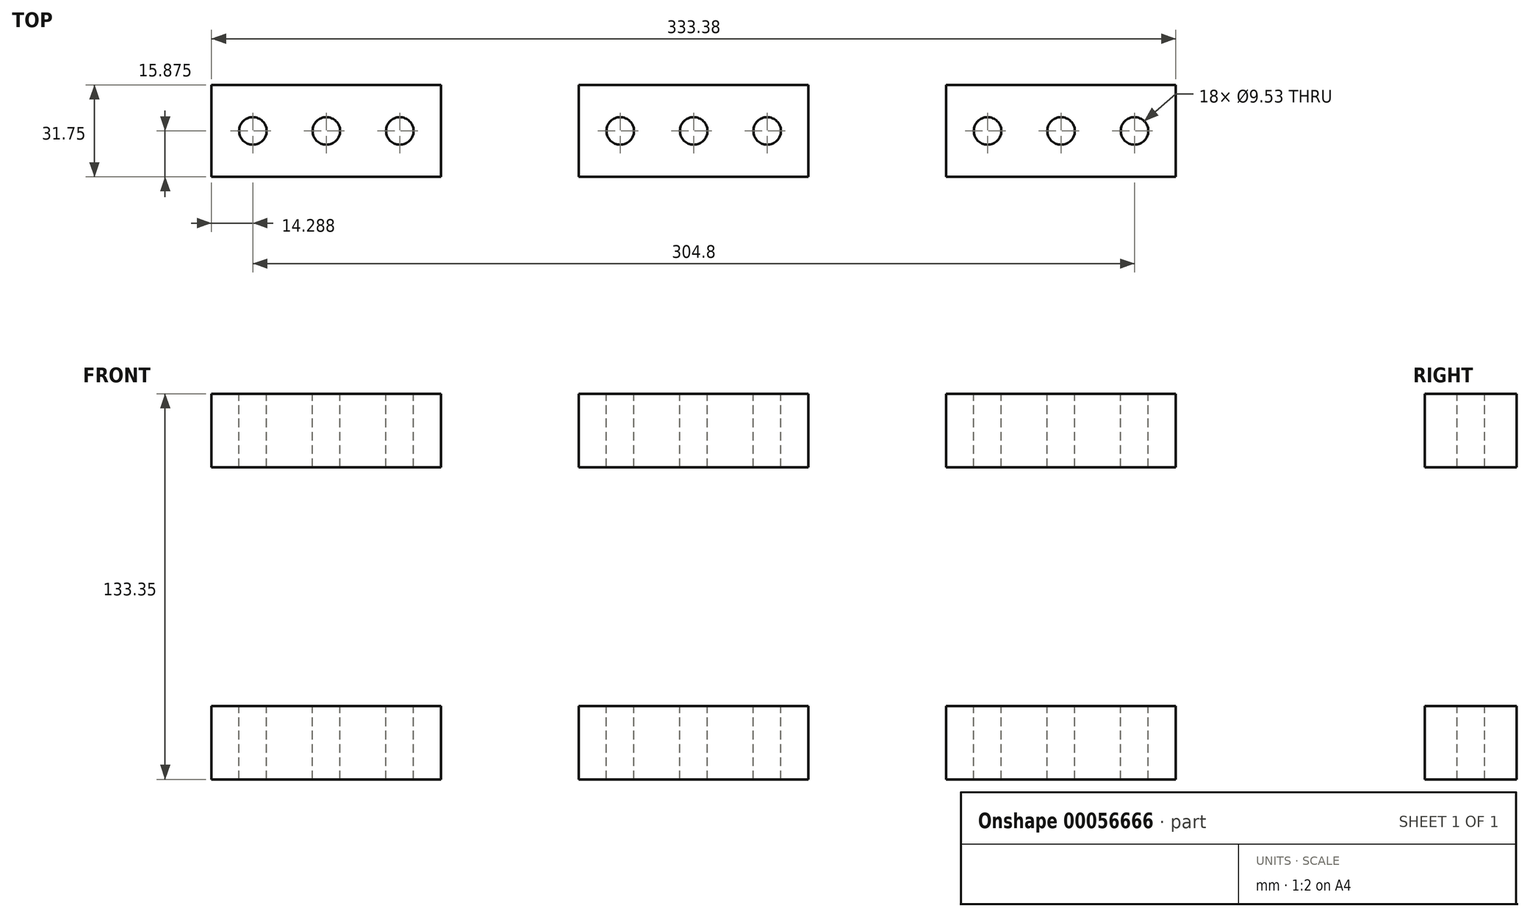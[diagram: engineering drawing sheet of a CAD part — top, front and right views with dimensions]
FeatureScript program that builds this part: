
annotation { "Feature Type Name" : "Feature", "Feature Type Description" : "" }
export const myFeature = defineFeature(function(context is Context, id is Id, definition is map)
    precondition{}
    {
        {
            var Q0;
            Q0=qCreatedBy(makeId("Front.planeOp"),FACE);
            cPlane(context, id + "F0", {"entities" : qUnion([Q0]), "cplaneType" : CPlaneType.OFFSET, "offset" : 152.4 * mm, "oppositeDirection" : true, "width" : 152.4 * mm, "height" : 152.4 * mm});
        }
        {
            var Q0;
            Q0=qCreatedBy(id+"F0.planeOp",FACE);
            var sketch = newSketch(context, id + "F1", { "sketchPlane" : qUnion([Q0])});
            skLineSegment(sketch, "E0.bottom", {"start": v(203.2, 742.95) * mm, "end": v(282.57, 742.95) * mm});
            skLineSegment(sketch, "E0.top", {"start": v(203.2, 717.55) * mm, "end": v(282.57, 717.55) * mm});
            skLineSegment(sketch, "E0.left", {"start": v(203.2, 742.95) * mm, "end": v(203.2, 717.55) * mm});
            skLineSegment(sketch, "E0.right", {"start": v(282.57, 742.95) * mm, "end": v(282.57, 717.55) * mm});
            skLineSegment(sketch, "E1.bottom", {"start": v(330.2, 742.95) * mm, "end": v(409.58, 742.95) * mm});
            skLineSegment(sketch, "E1.top", {"start": v(330.2, 717.55) * mm, "end": v(409.58, 717.55) * mm});
            skLineSegment(sketch, "E1.left", {"start": v(330.2, 742.95) * mm, "end": v(330.2, 717.55) * mm});
            skLineSegment(sketch, "E1.right", {"start": v(409.58, 742.95) * mm, "end": v(409.58, 717.55) * mm});
            skLineSegment(sketch, "E2.bottom", {"start": v(457.2, 742.95) * mm, "end": v(536.58, 742.95) * mm});
            skLineSegment(sketch, "E2.top", {"start": v(457.2, 717.55) * mm, "end": v(536.58, 717.55) * mm});
            skLineSegment(sketch, "E2.left", {"start": v(457.2, 742.95) * mm, "end": v(457.2, 717.55) * mm});
            skLineSegment(sketch, "E2.right", {"start": v(536.58, 742.95) * mm, "end": v(536.58, 717.55) * mm});
            skLineSegment(sketch, "E3.bottom", {"start": v(203.2, 635) * mm, "end": v(282.58, 635) * mm});
            skLineSegment(sketch, "E3.top", {"start": v(203.2, 609.6) * mm, "end": v(282.58, 609.6) * mm});
            skLineSegment(sketch, "E3.left", {"start": v(203.2, 635) * mm, "end": v(203.2, 609.6) * mm});
            skLineSegment(sketch, "E3.right", {"start": v(282.58, 635) * mm, "end": v(282.58, 609.6) * mm});
            skLineSegment(sketch, "E4.bottom", {"start": v(330.2, 635) * mm, "end": v(409.58, 635) * mm});
            skLineSegment(sketch, "E4.top", {"start": v(330.2, 609.6) * mm, "end": v(409.58, 609.6) * mm});
            skLineSegment(sketch, "E4.left", {"start": v(330.2, 635) * mm, "end": v(330.2, 609.6) * mm});
            skLineSegment(sketch, "E4.right", {"start": v(409.58, 635) * mm, "end": v(409.58, 609.6) * mm});
            skLineSegment(sketch, "E5.bottom", {"start": v(457.2, 635) * mm, "end": v(536.58, 635) * mm});
            skLineSegment(sketch, "E5.top", {"start": v(457.2, 609.6) * mm, "end": v(536.58, 609.6) * mm});
            skLineSegment(sketch, "E5.left", {"start": v(457.2, 635) * mm, "end": v(457.2, 609.6) * mm});
            skLineSegment(sketch, "E5.right", {"start": v(536.58, 635) * mm, "end": v(536.58, 609.6) * mm});
            skSolve(sketch);
        }
        {
            var Q0;
            Q0=makeQuery(id+"F1.imprint","IMPRINT",FACE,{"disambiguationData":[TD([[makeQuery(id+"F1.imprint","IMPRINT",EDGE,{"derivedFrom":sQuery(id+"F1.wireOp",EDGE,"E0.bottom")}),-1.0]])]});
            var Q1;
            Q1=makeQuery(id+"F1.imprint","IMPRINT",FACE,{"disambiguationData":[TD([[makeQuery(id+"F1.imprint","IMPRINT",EDGE,{"derivedFrom":sQuery(id+"F1.wireOp",EDGE,"E1.bottom")}),-1.0]])]});
            var Q2;
            Q2=makeQuery(id+"F1.imprint","IMPRINT",FACE,{"disambiguationData":[TD([[makeQuery(id+"F1.imprint","IMPRINT",EDGE,{"derivedFrom":sQuery(id+"F1.wireOp",EDGE,"E2.bottom")}),-1.0]])]});
            var Q3;
            Q3=makeQuery(id+"F1.imprint","IMPRINT",FACE,{"disambiguationData":[TD([[makeQuery(id+"F1.imprint","IMPRINT",EDGE,{"derivedFrom":sQuery(id+"F1.wireOp",EDGE,"E3.bottom")}),-1.0]])]});
            var Q4;
            Q4=makeQuery(id+"F1.imprint","IMPRINT",FACE,{"disambiguationData":[TD([[makeQuery(id+"F1.imprint","IMPRINT",EDGE,{"derivedFrom":sQuery(id+"F1.wireOp",EDGE,"E4.bottom")}),-1.0]])]});
            var Q5;
            Q5=makeQuery(id+"F1.imprint","IMPRINT",FACE,{"disambiguationData":[TD([[makeQuery(id+"F1.imprint","IMPRINT",EDGE,{"derivedFrom":sQuery(id+"F1.wireOp",EDGE,"E5.bottom")}),-1.0]])]});
            extrude(context, id + "F2", {"entities" : qUnion([Q0, Q1, Q2, Q3, Q4, Q5]), "depth" : 31.75 * mm});
        }
        {
            var Q0;
            Q0=makeQuery(id+"F2.opExtrude","SWEPT_FACE",FACE,{"disambiguationData":[OSD([sQuery(id+"F1.wireOp",EDGE,"E0.bottom")])]});
            var sketch = newSketch(context, id + "F3", { "sketchPlane" : qUnion([Q0])});
            skCircle(sketch, "E6", {"center": v(217.49, 136.53) * mm, "radius": 4.76 * mm});
            skCircle(sketch, "E7.1.0.0", {"center": v(242.89, 136.52) * mm, "radius": 4.76 * mm});
            skCircle(sketch, "E7.2.0.0", {"center": v(268.29, 136.53) * mm, "radius": 4.76 * mm});
            skLineSegment(sketch, "E7.direction1", {"start": v(217.49, 136.53) * mm, "end": v(242.89, 136.53) * mm, "construction": true});
            skCircle(sketch, "E8", {"center": v(344.49, 136.53) * mm, "radius": 4.76 * mm});
            skCircle(sketch, "E9.1.0.0", {"center": v(369.89, 136.53) * mm, "radius": 4.76 * mm});
            skCircle(sketch, "E9.2.0.0", {"center": v(395.29, 136.53) * mm, "radius": 4.76 * mm});
            skLineSegment(sketch, "E9.direction1", {"start": v(344.49, 136.53) * mm, "end": v(369.89, 136.53) * mm, "construction": true});
            skCircle(sketch, "E10", {"center": v(471.49, 136.53) * mm, "radius": 4.76 * mm});
            skCircle(sketch, "E11.1.0.0", {"center": v(496.89, 136.53) * mm, "radius": 4.76 * mm});
            skCircle(sketch, "E11.2.0.0", {"center": v(522.29, 136.53) * mm, "radius": 4.76 * mm});
            skLineSegment(sketch, "E11.direction1", {"start": v(471.49, 136.53) * mm, "end": v(496.89, 136.53) * mm, "construction": true});
            skSolve(sketch);
        }
        {
            var Q0;
            Q0 = qSketchRegion(id + "F3", true);
            extrude(context, id + "F4", {"entities" : qUnion([Q0]), "operationType" : NewBodyOperationType.REMOVE, "endBound" : BoundingType.THROUGH_ALL, "oppositeDirection" : true, "depth" : 25.4 * mm});
        }
    });
